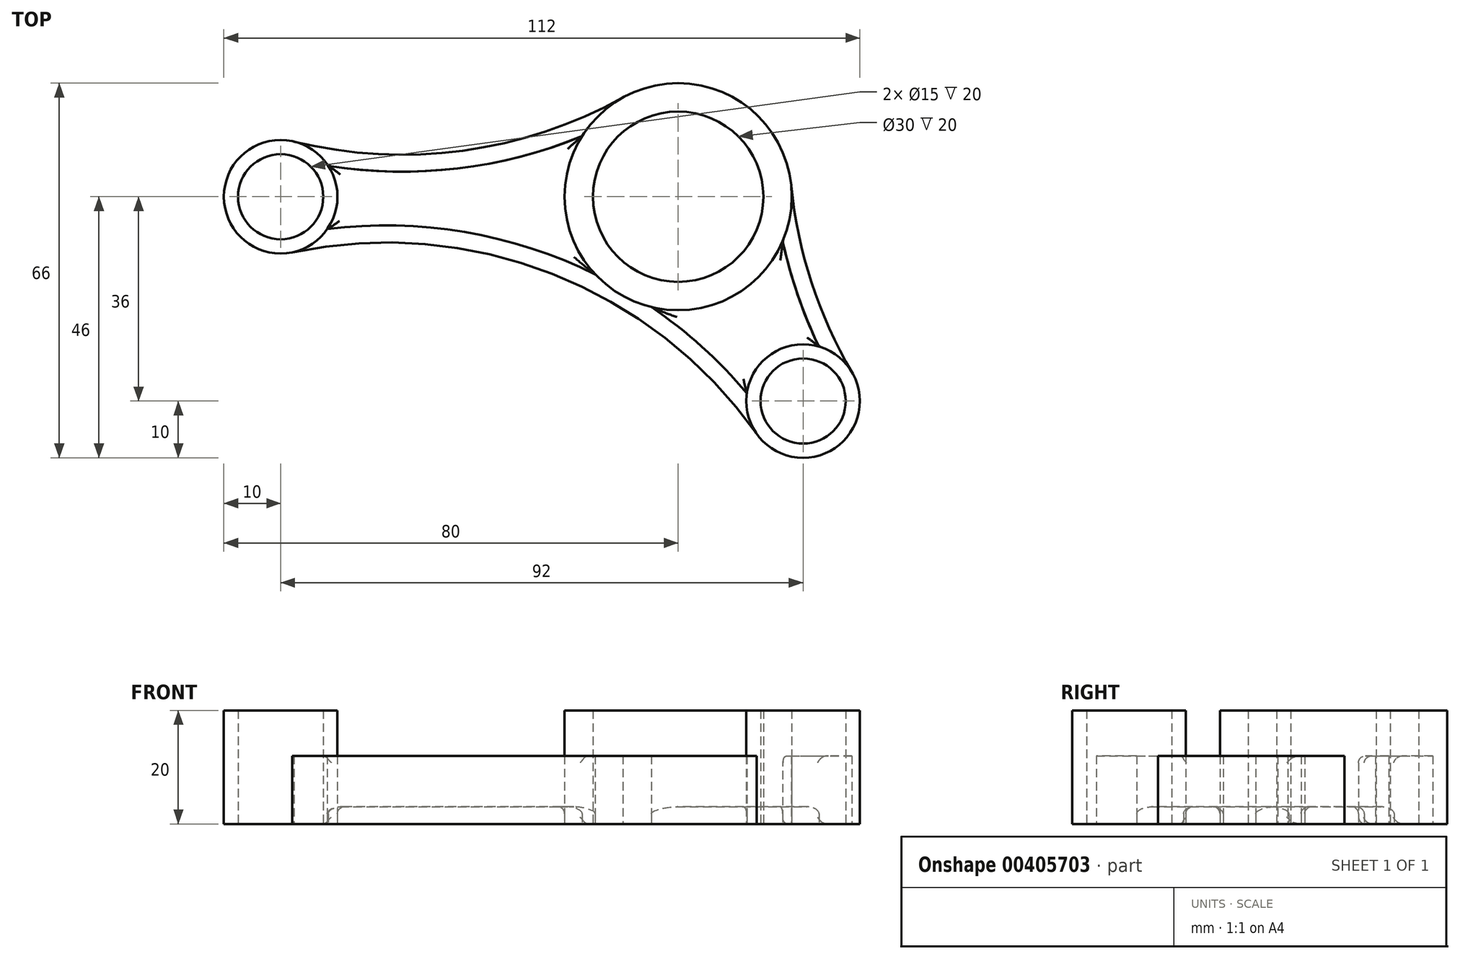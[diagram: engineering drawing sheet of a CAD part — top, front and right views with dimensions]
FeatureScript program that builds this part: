
annotation { "Feature Type Name" : "Feature", "Feature Type Description" : "" }
export const myFeature = defineFeature(function(context is Context, id is Id, definition is map)
    precondition{}
    {
        {
            var Q0;
            Q0=qCreatedBy(makeId("Top.planeOp"),FACE);
            var sketch = newSketch(context, id + "F0", { "sketchPlane" : qUnion([Q0])});
            skCircle(sketch, "E0", {"center": v(0, 0) * mm, "radius": 20 * mm});
            skCircle(sketch, "E1", {"center": v(-70, 0) * mm, "radius": 10 * mm});
            skCircle(sketch, "E2", {"center": v(22, -36) * mm, "radius": 10 * mm});
            skCircle(sketch, "E3.0", {"center": v(0, 0) * mm, "radius": 15 * mm});
            skCircle(sketch, "E4.0", {"center": v(22, -36) * mm, "radius": 7.5 * mm});
            skCircle(sketch, "E5.0", {"center": v(-70, 0) * mm, "radius": 7.5 * mm});
            skArc(sketch, "E6", {"start": v(-67.62, 9.71) * mm, "mid": v(-37.93, 8.12) * mm, "end": v(-9.71, 17.48) * mm});
            skArc(sketch, "E7", {"start": v(13.84, -41.78) * mm, "mid": v(-22.26, -13.56) * mm, "end": v(-67.93, -9.78) * mm});
            skArc(sketch, "E8", {"start": v(19.9, 1.94) * mm, "mid": v(23.46, -15.07) * mm, "end": v(30.61, -30.92) * mm});
            skArc(sketch, "E9.0", {"start": v(-61.61, 5.44) * mm, "mid": v(-38.9, 4.98) * mm, "end": v(-16.9, 10.7) * mm});
            skArc(sketch, "E10.0", {"start": v(12.1, -34.62) * mm, "mid": v(4.2, -26.45) * mm, "end": v(-4.73, -19.43) * mm});
            skArc(sketch, "E11.0", {"start": v(18.4, -7.83) * mm, "mid": v(21.05, -17.3) * mm, "end": v(24.8, -26.4) * mm});
            skArc(sketch, "E12.trimOffspring", {"start": v(-14.6, -13.67) * mm, "mid": v(-37.6, -6.22) * mm, "end": v(-61.8, -5.71) * mm});
            skSolve(sketch);
        }
        {
            var Q0;
            Q0=makeQuery(id+"F0.imprint","IMPRINT",FACE,{"disambiguationData":[TD([[makeQuery(id+"F0.imprint","IMPRINT",EDGE,{"derivedFrom":sQuery(id+"F0.wireOp",EDGE,"E1")}),1.0]])]});
            var Q1;
            Q1=makeQuery(id+"F0.imprint","IMPRINT",FACE,{"disambiguationData":[TD([[makeQuery(id+"F0.imprint","IMPRINT",EDGE,{"derivedFrom":sQuery(id+"F0.wireOp",EDGE,"E0")}),1.0]])]});
            var Q2;
            Q2=makeQuery(id+"F0.imprint","IMPRINT",FACE,{"disambiguationData":[TD([[makeQuery(id+"F0.imprint","IMPRINT",EDGE,{"derivedFrom":sQuery(id+"F0.wireOp",EDGE,"E2")}),1.0]])]});
            extrude(context, id + "F1", {"entities" : qUnion([Q0, Q1, Q2]), "depth" : 20 * mm});
        }
        {
            var Q0;
            {var subQ0=sQuery(id+"F0.wireOp",EDGE,"E6");Q0=makeQuery(id+"F0.imprint","IMPRINT",FACE,{"disambiguationData":[TD([[makeQuery(id+"F0.imprint","IMPRINT",EDGE,{"derivedFrom":subQ0}),-1.0]])]});}
            var Q1;
            {var subQ0=sQuery(id+"F0.wireOp",EDGE,"E7");Q1=makeQuery(id+"F0.imprint","IMPRINT",FACE,{"disambiguationData":[TD([[makeQuery(id+"F0.imprint","IMPRINT",EDGE,{"derivedFrom":subQ0}),-1.0]])]});}
            var Q2;
            {var subQ0=sQuery(id+"F0.wireOp",EDGE,"E8");Q2=makeQuery(id+"F0.imprint","IMPRINT",FACE,{"disambiguationData":[TD([[makeQuery(id+"F0.imprint","IMPRINT",EDGE,{"derivedFrom":subQ0}),-1.0]])]});}
            extrude(context, id + "F2", {"entities" : qUnion([Q0, Q1, Q2]), "depth" : 12 * mm});
        }
        {
            var Q0;
            {var subQ0=sQuery(id+"F0.wireOp",EDGE,"E9.0");Q0=makeQuery(id+"F0.imprint","IMPRINT",FACE,{"disambiguationData":[TD([[makeQuery(id+"F0.imprint","IMPRINT",EDGE,{"derivedFrom":subQ0}),-1.0]])]});}
            var Q1;
            {var subQ0=sQuery(id+"F0.wireOp",EDGE,"E10.0");Q1=makeQuery(id+"F0.imprint","IMPRINT",FACE,{"disambiguationData":[TD([[makeQuery(id+"F0.imprint","IMPRINT",EDGE,{"derivedFrom":subQ0}),-1.0]])]});}
            extrude(context, id + "F3", {"entities" : qUnion([Q0, Q1]), "depth" : 3 * mm});
        }
        {
            var Q0;
            Q0=makeQuery(id+"F2.opExtrude","SWEPT_FACE",FACE,{"disambiguationData":[OSD([sQuery(id+"F0.wireOp",EDGE,"E12.trimOffspring")])]});
            var Q1;
            Q1=makeQuery(id+"F3.opExtrude","CAP_FACE",FACE,{"disambiguationData":[OSD([sQuery(id+"F0.wireOp",EDGE,"E0"),sQuery(id+"F0.wireOp",EDGE,"E1"),sQuery(id+"F0.wireOp",EDGE,"E9.0"),sQuery(id+"F0.wireOp",EDGE,"E12.trimOffspring")])],"isStart":false});
            var Q2;
            Q2=makeQuery(id+"F2.opExtrude","SWEPT_FACE",FACE,{"disambiguationData":[OSD([sQuery(id+"F0.wireOp",EDGE,"E9.0")])]});
            var Q3;
            Q3=makeQuery(id+"F3.opExtrude","CAP_FACE",FACE,{"disambiguationData":[OSD([sQuery(id+"F0.wireOp",EDGE,"E0"),sQuery(id+"F0.wireOp",EDGE,"E2"),sQuery(id+"F0.wireOp",EDGE,"E10.0"),sQuery(id+"F0.wireOp",EDGE,"E11.0")])],"isStart":false});
            var Q4;
            Q4=makeQuery(id+"F2.opExtrude","SWEPT_FACE",FACE,{"disambiguationData":[OSD([sQuery(id+"F0.wireOp",EDGE,"E10.0")])]});
            var Q5;
            Q5=makeQuery(id+"F2.opExtrude","SWEPT_FACE",FACE,{"disambiguationData":[OSD([sQuery(id+"F0.wireOp",EDGE,"E11.0")])]});
            fillet(context, id + "F4", {"entities" : qUnion([Q0, Q1, Q2, Q3, Q4, Q5]), "radius" : 1.2 * mm, "tangentPropagation" : true, "allowEdgeOverflow" : false});
        }
    });
